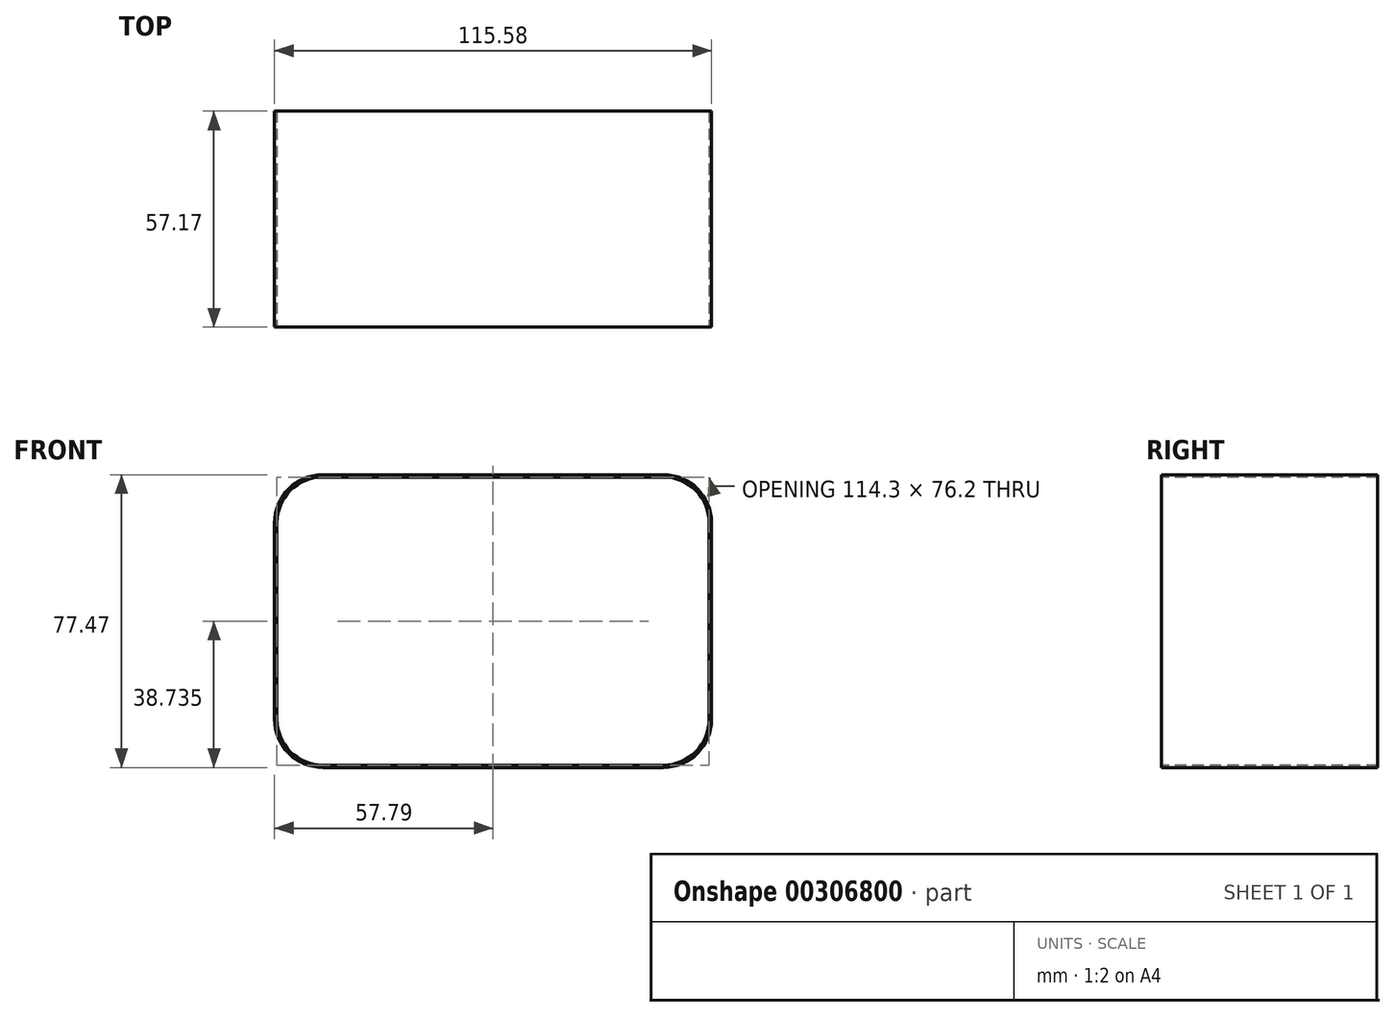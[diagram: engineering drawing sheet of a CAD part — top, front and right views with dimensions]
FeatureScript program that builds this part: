
annotation { "Feature Type Name" : "Feature", "Feature Type Description" : "" }
export const myFeature = defineFeature(function(context is Context, id is Id, definition is map)
    precondition{}
    {
        {
            var Q0;
            Q0=qCreatedBy(makeId("Top.planeOp"),FACE);
            var sketch = newSketch(context, id + "F0", { "sketchPlane" : qUnion([Q0])});
            skLineSegment(sketch, "E0.bottom", {"start": v(45.02, 38.73) * mm, "end": v(-45.02, 38.73) * mm});
            skLineSegment(sketch, "E0.top", {"start": v(45.02, -38.73) * mm, "end": v(-45.02, -38.73) * mm});
            skLineSegment(sketch, "E0.left", {"start": v(57.79, 25.97) * mm, "end": v(57.79, -25.97) * mm});
            skLineSegment(sketch, "E0.right", {"start": v(-57.79, 25.97) * mm, "end": v(-57.79, -25.97) * mm});
            skPoint(sketch, "E0.middle", {"position": v(0, 0) * mm});
            skPoint(sketch, "E1.visualSharp", {"position": v(-57.79, 38.73) * mm});
            skArc(sketch, "E1.filletArc", {"start": v(-45.02, 38.73) * mm, "mid": v(-54.05, 35) * mm, "end": v(-57.79, 25.97) * mm});
            skPoint(sketch, "E2.visualSharp", {"position": v(-57.79, -38.73) * mm});
            skArc(sketch, "E2.filletArc", {"start": v(-57.79, -25.97) * mm, "mid": v(-54.05, -35) * mm, "end": v(-45.02, -38.73) * mm});
            skPoint(sketch, "E3.visualSharp", {"position": v(57.79, -38.73) * mm});
            skArc(sketch, "E3.filletArc", {"start": v(45.02, -38.73) * mm, "mid": v(54.05, -35) * mm, "end": v(57.79, -25.97) * mm});
            skPoint(sketch, "E4.visualSharp", {"position": v(57.79, 38.73) * mm});
            skArc(sketch, "E4.filletArc", {"start": v(57.79, 25.97) * mm, "mid": v(54.05, 35) * mm, "end": v(45.02, 38.73) * mm});
            skSolve(sketch);
        }
        {
            var Q0;
            Q0=makeQuery(id+"F0.imprint","IMPRINT",FACE,{"disambiguationData":[TD([[makeQuery(id+"F0.imprint","IMPRINT",EDGE,{"derivedFrom":sQuery(id+"F0.wireOp",EDGE,"E0.bottom")}),1.0]])]});
            extrude(context, id + "F1", {"entities" : qUnion([Q0]), "depth" : 57.18 * mm});
        }
        {
            var Q0;
            Q0=makeQuery(id+"F1.opExtrude","CAP_FACE",FACE,{"disambiguationData":[OSD([sQuery(id+"F0.wireOp",EDGE,"E0.bottom"),sQuery(id+"F0.wireOp",EDGE,"E0.top"),sQuery(id+"F0.wireOp",EDGE,"E0.left"),sQuery(id+"F0.wireOp",EDGE,"E0.right"),sQuery(id+"F0.wireOp",EDGE,"E1.filletArc"),sQuery(id+"F0.wireOp",EDGE,"E2.filletArc"),sQuery(id+"F0.wireOp",EDGE,"E3.filletArc"),sQuery(id+"F0.wireOp",EDGE,"E4.filletArc")])],"isStart":false});
            var Q1;
            Q1=makeQuery(id+"F1.opExtrude","CAP_FACE",FACE,{"disambiguationData":[OSD([sQuery(id+"F0.wireOp",EDGE,"E0.bottom"),sQuery(id+"F0.wireOp",EDGE,"E0.top"),sQuery(id+"F0.wireOp",EDGE,"E0.left"),sQuery(id+"F0.wireOp",EDGE,"E0.right"),sQuery(id+"F0.wireOp",EDGE,"E1.filletArc"),sQuery(id+"F0.wireOp",EDGE,"E2.filletArc"),sQuery(id+"F0.wireOp",EDGE,"E3.filletArc"),sQuery(id+"F0.wireOp",EDGE,"E4.filletArc")])],"isStart":true});
            shell(context, id + "F2", {"entities" : qUnion([Q0, Q1]), "thickness" : 0.64 * mm});
        }
        {
            var Q0;
            Q0=makeQuery(id+"F1.opExtrude","SWEPT_BODY",BODY,{"disambiguationData":[OSD([sQuery(id+"F0.wireOp",EDGE,"E0.bottom"),sQuery(id+"F0.wireOp",EDGE,"E0.top"),sQuery(id+"F0.wireOp",EDGE,"E0.left"),sQuery(id+"F0.wireOp",EDGE,"E0.right"),sQuery(id+"F0.wireOp",EDGE,"E1.filletArc"),sQuery(id+"F0.wireOp",EDGE,"E2.filletArc"),sQuery(id+"F0.wireOp",EDGE,"E3.filletArc"),sQuery(id+"F0.wireOp",EDGE,"E4.filletArc")])]});
            var Q1;
            Q1=makeQuery(id+"F1.opExtrude","CAP_EDGE",EDGE,{"disambiguationData":[OSD([sQuery(id+"F0.wireOp",EDGE,"E0.top")])],"isStart":true});
            transform(context, id + "F3", {"entities" : qUnion([Q0]), "transformType" : TransformType.ROTATION, "transformAxis" : qUnion([Q1]), "angle" : 90 * degree, "makeCopy" : false});
        }
    });
